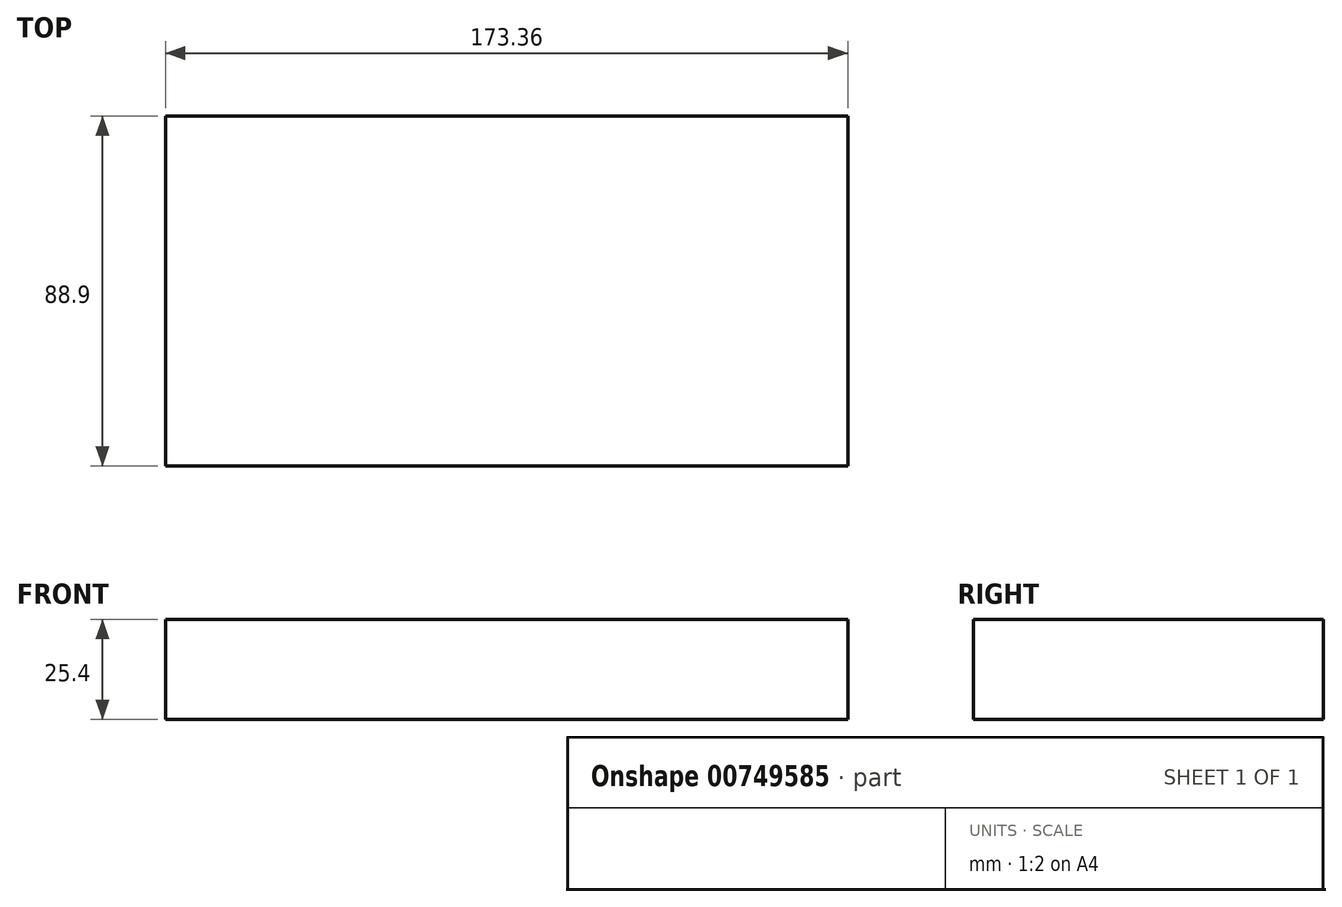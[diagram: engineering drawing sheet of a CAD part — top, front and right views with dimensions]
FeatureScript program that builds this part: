
annotation { "Feature Type Name" : "Feature", "Feature Type Description" : "" }
export const myFeature = defineFeature(function(context is Context, id is Id, definition is map)
    precondition{}
    {
        {
            var Q0;
            Q0=qCreatedBy(makeId("Top.planeOp"),FACE);
            var sketch = newSketch(context, id + "F0", { "sketchPlane" : qUnion([Q0])});
            skLineSegment(sketch, "E0.bottom", {"start": v(1.33, 0) * mm, "end": v(174.69, 0) * mm});
            skLineSegment(sketch, "E0.top", {"start": v(1.33, 88.9) * mm, "end": v(174.69, 88.9) * mm});
            skLineSegment(sketch, "E0.left", {"start": v(1.33, 0) * mm, "end": v(1.33, 88.9) * mm});
            skLineSegment(sketch, "E0.right", {"start": v(174.69, 0) * mm, "end": v(174.69, 88.9) * mm});
            skSolve(sketch);
        }
        {
            var Q0;
            Q0 = qSketchRegion(id + "F0", true);
            extrude(context, id + "F1", {"entities" : qUnion([Q0]), "depth" : 25.4 * mm, "offsetDistance" : 25.4 * mm});
        }
    });
